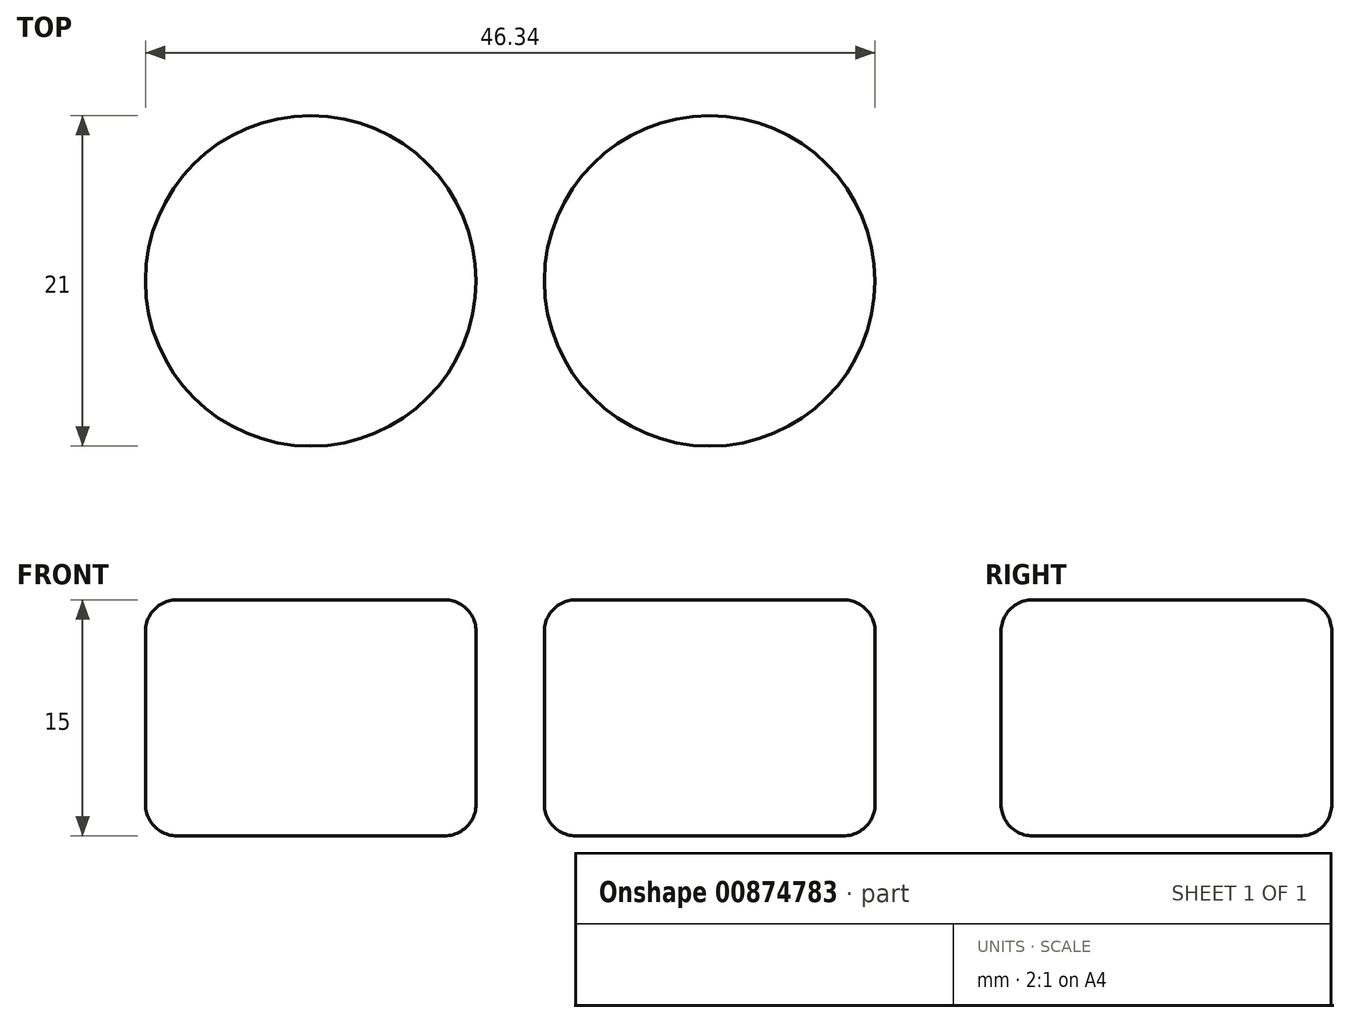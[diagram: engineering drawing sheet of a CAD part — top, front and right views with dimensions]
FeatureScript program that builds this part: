
annotation { "Feature Type Name" : "Feature", "Feature Type Description" : "" }
export const myFeature = defineFeature(function(context is Context, id is Id, definition is map)
    precondition{}
    {
        {
            var Q0;
            Q0=qCreatedBy(makeId("Top.planeOp"),FACE);
            var sketch = newSketch(context, id + "F0", { "sketchPlane" : qUnion([Q0])});
            skCircle(sketch, "E0", {"center": v(-51.67, 23.47) * mm, "radius": 10.5 * mm});
            skCircle(sketch, "E1.MirrorC", {"center": v(-26.33, 23.47) * mm, "radius": 10.5 * mm});
            skSolve(sketch);
        }
        {
            var Q0;
            Q0 = qSketchRegion(id + "F0", true);
            var Q1;
            Q1=makeQuery(id+"F0.imprint","IMPRINT",FACE,{"disambiguationData":[TD([[makeQuery(id+"F0.imprint","IMPRINT",EDGE,{"derivedFrom":sQuery(id+"F0.wireOp",EDGE,"E0")}),1.0]])]});
            extrude(context, id + "F1", {"entities" : qUnion([Q0, Q1]), "depth" : 15 * mm, "offsetDistance" : 25 * mm});
        }
        {
            var Q0;
            Q0=makeQuery(id+"F1.opExtrude","CAP_EDGE",EDGE,{"disambiguationData":[OSD([sQuery(id+"F0.wireOp",EDGE,"E1.MirrorC")])],"isStart":false});
            var Q1;
            Q1=makeQuery(id+"F1.opExtrude","CAP_EDGE",EDGE,{"disambiguationData":[OSD([sQuery(id+"F0.wireOp",EDGE,"E0")])],"isStart":false});
            var Q2;
            Q2=makeQuery(id+"F1.opExtrude","CAP_EDGE",EDGE,{"disambiguationData":[OSD([sQuery(id+"F0.wireOp",EDGE,"E0")])],"isStart":true});
            var Q3;
            Q3=makeQuery(id+"F1.opExtrude","CAP_EDGE",EDGE,{"disambiguationData":[OSD([sQuery(id+"F0.wireOp",EDGE,"E1.MirrorC")])],"isStart":true});
            fillet(context, id + "F2", {"entities" : qUnion([Q0, Q1, Q2, Q3]), "radius" : 2 * mm, "tangentPropagation" : true, "allowEdgeOverflow" : false});
        }
    });
